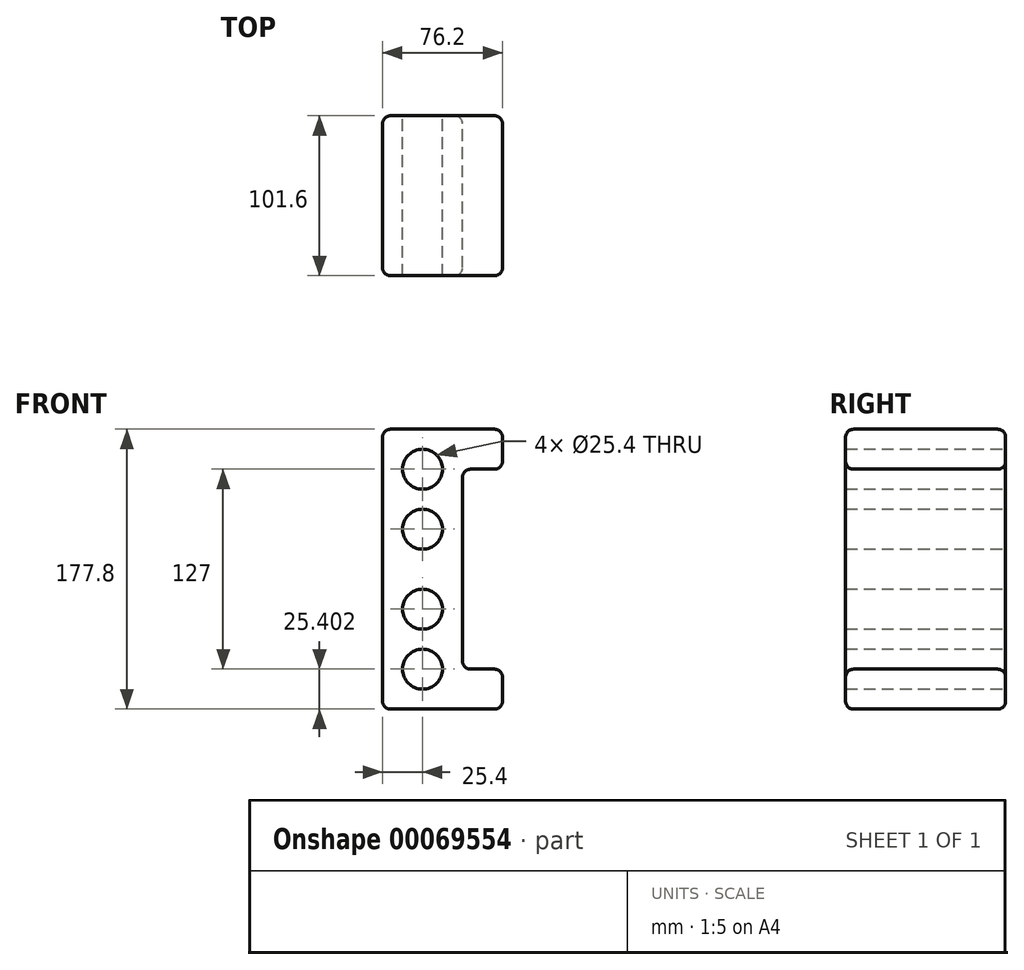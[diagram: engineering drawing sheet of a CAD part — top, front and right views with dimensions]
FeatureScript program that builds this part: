
annotation { "Feature Type Name" : "Feature", "Feature Type Description" : "" }
export const myFeature = defineFeature(function(context is Context, id is Id, definition is map)
    precondition{}
    {
        {
            var Q0;
            Q0=qCreatedBy(makeId("Front.planeOp"),FACE);
            var sketch = newSketch(context, id + "F0", { "sketchPlane" : qUnion([Q0])});
            skLineSegment(sketch, "E0", {"start": v(-47.1, 119.94) * mm, "end": v(29.1, 119.94) * mm});
            skLineSegment(sketch, "E1", {"start": v(29.1, 119.94) * mm, "end": v(29.1, 94.54) * mm});
            skLineSegment(sketch, "E2", {"start": v(29.1, 94.54) * mm, "end": v(3.7, 94.54) * mm});
            skLineSegment(sketch, "E3", {"start": v(3.7, 94.54) * mm, "end": v(3.7, -32.46) * mm});
            skLineSegment(sketch, "E4", {"start": v(3.7, -32.46) * mm, "end": v(29.1, -32.46) * mm});
            skLineSegment(sketch, "E5", {"start": v(29.1, -32.46) * mm, "end": v(29.1, -57.86) * mm});
            skLineSegment(sketch, "E6", {"start": v(29.1, -57.86) * mm, "end": v(-47.1, -57.86) * mm});
            skLineSegment(sketch, "E7", {"start": v(-47.1, -57.86) * mm, "end": v(-47.1, 119.94) * mm});
            skCircle(sketch, "E8", {"center": v(-21.7, 94.54) * mm, "radius": 12.7 * mm});
            skCircle(sketch, "E9", {"center": v(-21.7, -32.46) * mm, "radius": 12.7 * mm});
            skCircle(sketch, "E10", {"center": v(-21.7, 5.64) * mm, "radius": 12.7 * mm});
            skCircle(sketch, "E11", {"center": v(-21.7, 56.44) * mm, "radius": 12.7 * mm});
            skSolve(sketch);
        }
        {
            var Q0;
            Q0=makeQuery(id+"F0.imprint","IMPRINT",FACE,{"disambiguationData":[TD([[makeQuery(id+"F0.imprint","IMPRINT",EDGE,{"derivedFrom":sQuery(id+"F0.wireOp",EDGE,"E0")}),-1.0]])]});
            extrude(context, id + "F1", {"entities" : qUnion([Q0]), "depth" : 101.6 * mm});
        }
        {
            var Q0;
            Q0=makeQuery(id+"F1.opExtrude","CAP_EDGE",EDGE,{"disambiguationData":[OSD([sQuery(id+"F0.wireOp",EDGE,"E0")])],"isStart":false});
            var Q1;
            Q1=makeQuery(id+"F1.opExtrude","CAP_EDGE",EDGE,{"disambiguationData":[OSD([sQuery(id+"F0.wireOp",EDGE,"E7")])],"isStart":false});
            var Q2;
            Q2=makeQuery(id+"F1.opExtrude","CAP_EDGE",EDGE,{"disambiguationData":[OSD([sQuery(id+"F0.wireOp",EDGE,"E1")])],"isStart":false});
            var Q3;
            Q3=makeQuery(id+"F1.opExtrude","CAP_EDGE",EDGE,{"disambiguationData":[OSD([sQuery(id+"F0.wireOp",EDGE,"E2")])],"isStart":false});
            var Q4;
            Q4=makeQuery(id+"F1.opExtrude","CAP_EDGE",EDGE,{"disambiguationData":[OSD([sQuery(id+"F0.wireOp",EDGE,"E3")])],"isStart":false});
            var Q5;
            Q5=makeQuery(id+"F1.opExtrude","CAP_EDGE",EDGE,{"disambiguationData":[OSD([sQuery(id+"F0.wireOp",EDGE,"E4")])],"isStart":false});
            var Q6;
            Q6=makeQuery(id+"F1.opExtrude","CAP_EDGE",EDGE,{"disambiguationData":[OSD([sQuery(id+"F0.wireOp",EDGE,"E5")])],"isStart":false});
            var Q7;
            Q7=makeQuery(id+"F1.opExtrude","CAP_EDGE",EDGE,{"disambiguationData":[OSD([sQuery(id+"F0.wireOp",EDGE,"E6")])],"isStart":false});
            var Q8;
            Q8=makeQuery(id+"F1.opExtrude","SWEPT_EDGE",EDGE,{"disambiguationData":[OSD([sQuery(id+"F0.wireOp",EDGE,"E0"),sQuery(id+"F0.wireOp",EDGE,"E7")])]});
            var Q9;
            Q9=makeQuery(id+"F1.opExtrude","CAP_EDGE",EDGE,{"disambiguationData":[OSD([sQuery(id+"F0.wireOp",EDGE,"E0")])],"isStart":true});
            var Q10;
            Q10=makeQuery(id+"F1.opExtrude","SWEPT_EDGE",EDGE,{"disambiguationData":[OSD([sQuery(id+"F0.wireOp",EDGE,"E0"),sQuery(id+"F0.wireOp",EDGE,"E1")])]});
            var Q11;
            Q11=makeQuery(id+"F1.opExtrude","CAP_EDGE",EDGE,{"disambiguationData":[OSD([sQuery(id+"F0.wireOp",EDGE,"E7")])],"isStart":true});
            var Q12;
            Q12=makeQuery(id+"F1.opExtrude","SWEPT_EDGE",EDGE,{"disambiguationData":[OSD([sQuery(id+"F0.wireOp",EDGE,"E6"),sQuery(id+"F0.wireOp",EDGE,"E7")])]});
            var Q13;
            Q13=makeQuery(id+"F1.opExtrude","SWEPT_EDGE",EDGE,{"disambiguationData":[OSD([sQuery(id+"F0.wireOp",EDGE,"E4"),sQuery(id+"F0.wireOp",EDGE,"E5")])]});
            var Q14;
            Q14=makeQuery(id+"F1.opExtrude","SWEPT_EDGE",EDGE,{"disambiguationData":[OSD([sQuery(id+"F0.wireOp",EDGE,"E3"),sQuery(id+"F0.wireOp",EDGE,"E4")])]});
            var Q15;
            Q15=makeQuery(id+"F1.opExtrude","SWEPT_EDGE",EDGE,{"disambiguationData":[OSD([sQuery(id+"F0.wireOp",EDGE,"E1"),sQuery(id+"F0.wireOp",EDGE,"E2")])]});
            var Q16;
            Q16=makeQuery(id+"F1.opExtrude","CAP_EDGE",EDGE,{"disambiguationData":[OSD([sQuery(id+"F0.wireOp",EDGE,"E1")])],"isStart":true});
            var Q17;
            Q17=makeQuery(id+"F1.opExtrude","SWEPT_EDGE",EDGE,{"disambiguationData":[OSD([sQuery(id+"F0.wireOp",EDGE,"E5"),sQuery(id+"F0.wireOp",EDGE,"E6")])]});
            var Q18;
            Q18=makeQuery(id+"F1.opExtrude","CAP_EDGE",EDGE,{"disambiguationData":[OSD([sQuery(id+"F0.wireOp",EDGE,"E5")])],"isStart":true});
            var Q19;
            Q19=makeQuery(id+"F1.opExtrude","SWEPT_EDGE",EDGE,{"disambiguationData":[OSD([sQuery(id+"F0.wireOp",EDGE,"E2"),sQuery(id+"F0.wireOp",EDGE,"E3")])]});
            var Q20;
            Q20=makeQuery(id+"F1.opExtrude","CAP_EDGE",EDGE,{"disambiguationData":[OSD([sQuery(id+"F0.wireOp",EDGE,"E2")])],"isStart":true});
            var Q21;
            Q21=makeQuery(id+"F1.opExtrude","CAP_EDGE",EDGE,{"disambiguationData":[OSD([sQuery(id+"F0.wireOp",EDGE,"E3")])],"isStart":true});
            var Q22;
            Q22=makeQuery(id+"F1.opExtrude","CAP_EDGE",EDGE,{"disambiguationData":[OSD([sQuery(id+"F0.wireOp",EDGE,"E4")])],"isStart":true});
            var Q23;
            Q23=makeQuery(id+"F1.opExtrude","CAP_EDGE",EDGE,{"disambiguationData":[OSD([sQuery(id+"F0.wireOp",EDGE,"E6")])],"isStart":true});
            fillet(context, id + "F2", {"entities" : qUnion([Q0, Q1, Q2, Q3, Q4, Q5, Q6, Q7, Q8, Q9, Q10, Q11, Q12, Q13, Q14, Q15, Q16, Q17, Q18, Q19, Q20, Q21, Q22, Q23]), "radius" : 5.08 * mm, "tangentPropagation" : true, "allowEdgeOverflow" : false});
        }
    });
